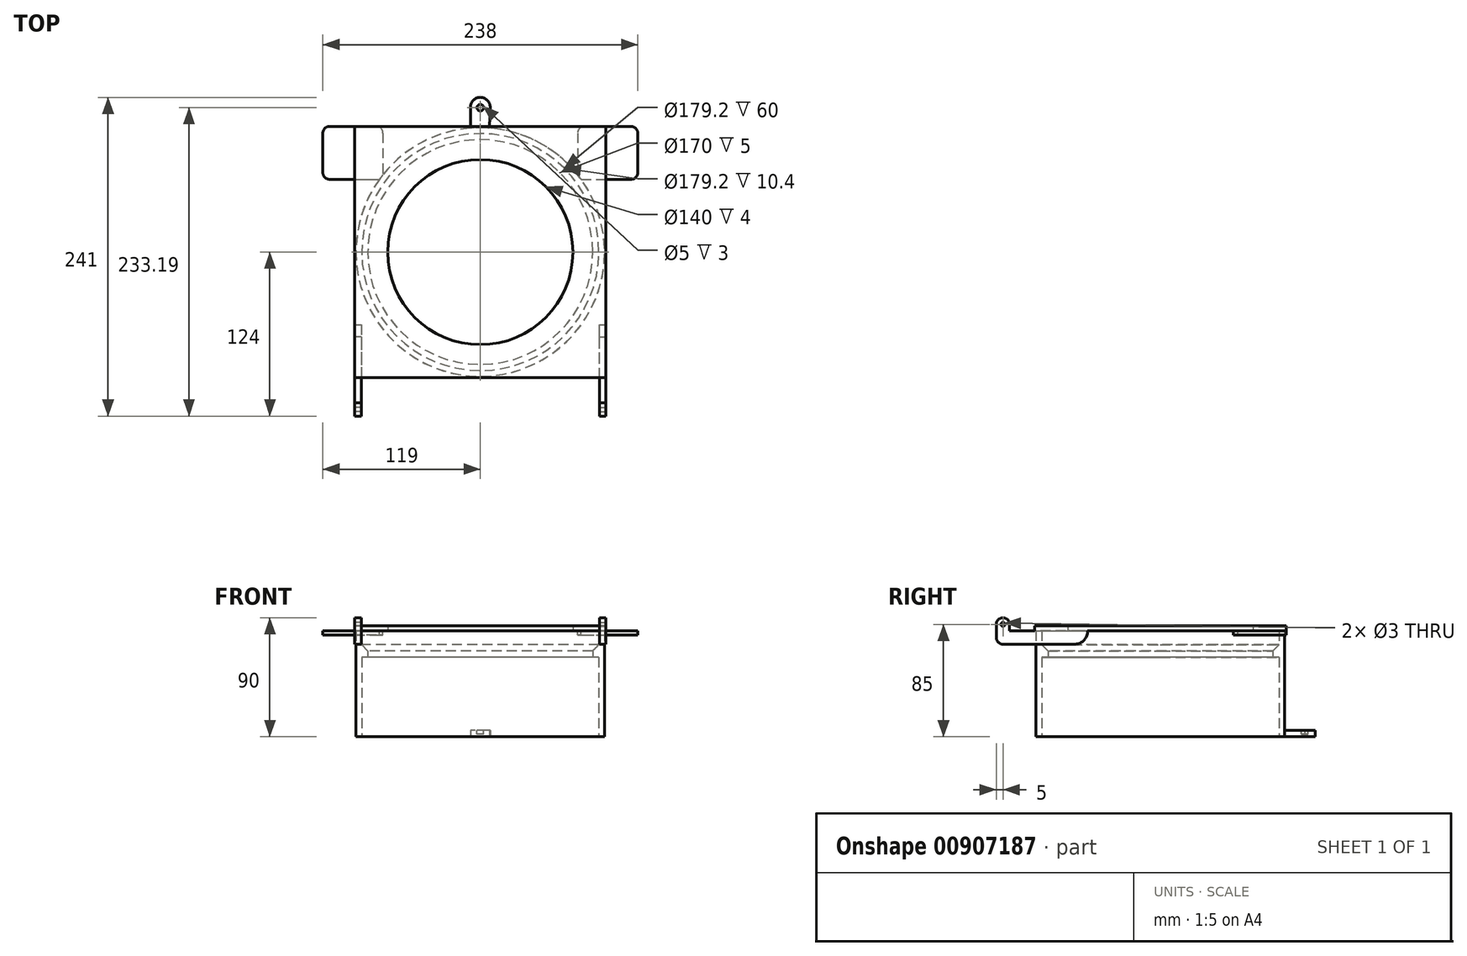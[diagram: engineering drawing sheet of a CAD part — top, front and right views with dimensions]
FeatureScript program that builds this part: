
annotation { "Feature Type Name" : "Feature", "Feature Type Description" : "" }
export const myFeature = defineFeature(function(context is Context, id is Id, definition is map)
    precondition{}
    {
        {
            var Q0;
            Q0=qCreatedBy(makeId("Top.planeOp"),FACE);
            var sketch = newSketch(context, id + "F0", { "sketchPlane" : qUnion([Q0])});
            skCircle(sketch, "E0", {"center": v(0, 0) * mm, "radius": 94 * mm});
            skCircle(sketch, "E1", {"center": v(0, 0) * mm, "radius": 89.6 * mm});
            skArc(sketch, "E2", {"start": v(7.5, 109.26) * mm, "mid": v(-0.04, 117) * mm, "end": v(-7.5, 109.19) * mm});
            skLineSegment(sketch, "E3", {"start": v(-7.5, 109.19) * mm, "end": v(-7.5, 93.7) * mm});
            skLineSegment(sketch, "E4", {"start": v(7.5, 109.26) * mm, "end": v(7, 93.74) * mm});
            skSolve(sketch);
        }
        {
            var Q0;
            Q0=makeQuery(id+"F0.imprint","IMPRINT",FACE,{"disambiguationData":[TD([[makeQuery(id+"F0.imprint","IMPRINT",EDGE,{"derivedFrom":sQuery(id+"F0.wireOp",EDGE,"E0")}),1.0]])]});
            extrude(context, id + "F1", {"entities" : qUnion([Q0]), "depth" : 60 * mm});
        }
        {
            var Q0;
            Q0=makeQuery(id+"F1.opExtrude","CAP_FACE",FACE,{"disambiguationData":[OSD([sQuery(id+"F0.wireOp",EDGE,"E0"),sQuery(id+"F0.wireOp",EDGE,"E1")])],"isStart":false});
            var sketch = newSketch(context, id + "F2", { "sketchPlane" : qUnion([Q0])});
            skCircle(sketch, "E5", {"center": v(0, 0) * mm, "radius": 94 * mm});
            skCircle(sketch, "E6", {"center": v(0, 0) * mm, "radius": 85 * mm});
            skSolve(sketch);
        }
        {
            var Q0;
            Q0=makeQuery(id+"F2.imprint","IMPRINT",FACE,{"disambiguationData":[TD([[makeQuery(id+"F2.imprint","IMPRINT",EDGE,{"derivedFrom":sQuery(id+"F2.wireOp",EDGE,"E6")}),-1.0]])]});
            var Q1;
            Q1=makeQuery(id+"F2.imprint","IMPRINT",FACE,{"disambiguationData":[TD([[makeQuery(id+"F2.imprint","IMPRINT",EDGE,{"derivedFrom":sQuery(id+"F2.wireOp",EDGE,"E5")}),1.0]])]});
            extrude(context, id + "F3", {"entities" : qUnion([Q0, Q1]), "operationType" : NewBodyOperationType.ADD, "depth" : 10 * mm});
        }
        {
            var Q0;
            Q0=makeQuery(id+"F3.opExtrude","CAP_FACE",FACE,{"disambiguationData":[OSD([sQuery(id+"F2.wireOp",EDGE,"E5"),sQuery(id+"F2.wireOp",EDGE,"E6")])],"isStart":false});
            var sketch = newSketch(context, id + "F4", { "sketchPlane" : qUnion([Q0])});
            skCircle(sketch, "E7", {"center": v(0, 0) * mm, "radius": 94 * mm});
            skCircle(sketch, "E8", {"center": v(0, 0) * mm, "radius": 89.6 * mm});
            skSolve(sketch);
        }
        {
            var Q0;
            Q0=makeQuery(id+"F4.imprint","IMPRINT",FACE,{"disambiguationData":[TD([[makeQuery(id+"F4.imprint","IMPRINT",EDGE,{"derivedFrom":sQuery(id+"F4.wireOp",EDGE,"E7")}),1.0]])]});
            extrude(context, id + "F5", {"entities" : qUnion([Q0]), "operationType" : NewBodyOperationType.ADD, "depth" : 10 * mm});
        }
        {
            var Q0;
            Q0=makeQuery(id+"F5.opExtrude","CAP_FACE",FACE,{"disambiguationData":[OSD([sQuery(id+"F4.wireOp",EDGE,"E7"),sQuery(id+"F4.wireOp",EDGE,"E8")])],"isStart":false});
            var sketch = newSketch(context, id + "F6", { "sketchPlane" : qUnion([Q0])});
            skLineSegment(sketch, "E9.bottom", {"start": v(95, -95) * mm, "end": v(-95, -95) * mm});
            skLineSegment(sketch, "E9.top", {"start": v(95, 95) * mm, "end": v(-95, 95) * mm});
            skLineSegment(sketch, "E9.left", {"start": v(95, -95) * mm, "end": v(95, 95) * mm});
            skLineSegment(sketch, "E9.right", {"start": v(-95, -95) * mm, "end": v(-95, 95) * mm});
            skPoint(sketch, "E9.middle", {"position": v(0, 0) * mm});
            skCircle(sketch, "E10", {"center": v(0, 0) * mm, "radius": 70 * mm});
            skSolve(sketch);
        }
        {
            var Q0;
            Q0=makeQuery(id+"F6.imprint","IMPRINT",FACE,{"disambiguationData":[TD([[makeQuery(id+"F6.imprint","IMPRINT",EDGE,{"derivedFrom":sQuery(id+"F6.wireOp",EDGE,"E9.bottom")}),-1.0]])]});
            var Q1;
            Q1=makeQuery(id+"F6.imprint","IMPRINT",FACE,{"disambiguationData":[TD([[makeQuery(id+"F6.imprint","IMPRINT",EDGE,{"derivedFrom":sQuery(id+"F6.wireOp",EDGE,"E10")}),-1.0]])]});
            var Q2;
            Q2=makeQuery(id+"F6.imprint","IMPRINT",FACE,{"disambiguationData":[TD([[makeQuery(id+"F6.imprint","IMPRINT",EDGE,{"derivedFrom":makeQuery(id+"F5.opExtrude","CAP_EDGE",EDGE,{"disambiguationData":[OSD([sQuery(id+"F4.wireOp",EDGE,"E7")])],"isStart":false})}),1.0]])]});
            extrude(context, id + "F7", {"entities" : qUnion([Q0, Q1, Q2]), "operationType" : NewBodyOperationType.ADD, "depth" : 4 * mm});
        }
        {
            var Q0;
            Q0=makeQuery(id+"F0.imprint","IMPRINT",FACE,{"disambiguationData":[TD([[makeQuery(id+"F0.imprint","IMPRINT",EDGE,{"derivedFrom":sQuery(id+"F0.wireOp",EDGE,"E2")}),1.0]])]});
            extrude(context, id + "F8", {"entities" : qUnion([Q0]), "operationType" : NewBodyOperationType.ADD, "depth" : 5 * mm});
        }
        {
            var Q0;
            Q0=makeQuery(id+"F8.opExtrude","CAP_FACE",FACE,{"disambiguationData":[OSD([sQuery(id+"F0.wireOp",EDGE,"E0"),sQuery(id+"F0.wireOp",EDGE,"E2"),sQuery(id+"F0.wireOp",EDGE,"E3"),sQuery(id+"F0.wireOp",EDGE,"E4")])],"isStart":false});
            var sketch = newSketch(context, id + "F9", { "sketchPlane" : qUnion([Q0])});
            skCircle(sketch, "E11", {"center": v(0, 109.19) * mm, "radius": 2.5 * mm});
            skSolve(sketch);
        }
        {
            var Q0;
            Q0=makeQuery(id+"F9.imprint","IMPRINT",FACE,{"disambiguationData":[TD([[makeQuery(id+"F9.imprint","IMPRINT",EDGE,{"derivedFrom":sQuery(id+"F9.wireOp",EDGE,"E11")}),1.0]])]});
            extrude(context, id + "F10", {"entities" : qUnion([Q0]), "operationType" : NewBodyOperationType.REMOVE, "oppositeDirection" : true, "depth" : 3 * mm});
        }
        {
            var Q0;
            Q0=makeQuery(id+"F3.opExtrude","CAP_EDGE",EDGE,{"disambiguationData":[OSD([sQuery(id+"F2.wireOp",EDGE,"E6")])],"isStart":false});
            chamfer(context, id + "F11", {"entities" : qUnion([Q0]), "width" : 5 * mm, "tangentPropagation" : true});
        }
        {
            var Q0;
            {var subQ0=sQuery(id+"F6.wireOp",EDGE,"E9.bottom");var subQ1=sQuery(id+"F6.wireOp",EDGE,"E9.top");var subQ2=sQuery(id+"F6.wireOp",EDGE,"E9.left");var subQ3=sQuery(id+"F6.wireOp",EDGE,"E9.right");Q0=makeQuery(id+"F7.boolean.opBoolean","SPLIT",FACE,{"disambiguationData":[TD([makeQuery(id+"F1.opExtrude","SWEPT_FACE",FACE,{"disambiguationData":[OSD([sQuery(id+"F0.wireOp",EDGE,"E0")])]})])],"derivedFrom":makeQuery(id+"F7.opExtrude","CAP_FACE",FACE,{"disambiguationData":[OSD([subQ0,subQ1,subQ2,subQ3,sQuery(id+"F6.wireOp",EDGE,"E10")])],"isStart":true})});}
            var sketch = newSketch(context, id + "F12", { "sketchPlane" : qUnion([Q0])});
            skLineSegment(sketch, "E12.bottom", {"start": v(95, -95) * mm, "end": v(114, -95) * mm});
            skLineSegment(sketch, "E12.top", {"start": v(95, -55) * mm, "end": v(114, -55) * mm});
            skLineSegment(sketch, "E12.right", {"start": v(119, -90) * mm, "end": v(119, -60) * mm});
            skPoint(sketch, "E13.visualSharp", {"position": v(119, -95) * mm});
            skArc(sketch, "E13.filletArc", {"start": v(114, -95) * mm, "mid": v(117.54, -93.54) * mm, "end": v(119, -90) * mm});
            skPoint(sketch, "E14.visualSharp", {"position": v(119, -55) * mm});
            skArc(sketch, "E14.filletArc", {"start": v(119, -60) * mm, "mid": v(117.54, -56.46) * mm, "end": v(114, -55) * mm});
            skLineSegment(sketch, "E15.bottom", {"start": v(95, -95) * mm, "end": v(78.59, -95) * mm});
            skLineSegment(sketch, "E15.top", {"start": v(95, -55) * mm, "end": v(73.59, -55) * mm});
            skLineSegment(sketch, "E15.right", {"start": v(73.59, -90) * mm, "end": v(73.59, -55) * mm});
            skPoint(sketch, "E16.visualSharp", {"position": v(73.59, -95) * mm});
            skArc(sketch, "E16.filletArc", {"start": v(73.59, -90) * mm, "mid": v(75.05, -93.54) * mm, "end": v(78.59, -95) * mm});
            skLineSegment(sketch, "E17.MirrorCS", {"start": v(-95, -95) * mm, "end": v(-114, -95) * mm});
            skLineSegment(sketch, "E18.MirrorCS", {"start": v(-95, -95) * mm, "end": v(-78.59, -95) * mm});
            skArc(sketch, "E19.MirrorCS", {"start": v(-73.59, -90) * mm, "mid": v(-75.05, -93.54) * mm, "end": v(-78.59, -95) * mm});
            skLineSegment(sketch, "E20.MirrorCS", {"start": v(-73.59, -90) * mm, "end": v(-73.59, -55) * mm});
            skLineSegment(sketch, "E21.MirrorCS", {"start": v(-95, -55) * mm, "end": v(-73.59, -55) * mm});
            skLineSegment(sketch, "E22.MirrorCS", {"start": v(-95, -55) * mm, "end": v(-114, -55) * mm});
            skArc(sketch, "E23.MirrorCS", {"start": v(-119, -60) * mm, "mid": v(-117.54, -56.46) * mm, "end": v(-114, -55) * mm});
            skLineSegment(sketch, "E24.MirrorCS", {"start": v(-119, -90) * mm, "end": v(-119, -60) * mm});
            skArc(sketch, "E25.MirrorCS", {"start": v(-114, -95) * mm, "mid": v(-117.54, -93.54) * mm, "end": v(-119, -90) * mm});
            skSolve(sketch);
        }
        {
            var Q0;
            {var subQ1=sQuery(id+"F12.wireOp",EDGE,"E12.bottom");Q0=makeQuery(id+"F12.imprint","IMPRINT",FACE,{"disambiguationData":[TD([[makeQuery(id+"F12.imprint","IMPRINT",EDGE,{"derivedFrom":subQ1}),1.0]])]});}
            var Q1;
            {var subQ8=sQuery(id+"F12.wireOp",EDGE,"E15.bottom");Q1=makeQuery(id+"F12.imprint","IMPRINT",FACE,{"disambiguationData":[TD([[makeQuery(id+"F12.imprint","IMPRINT",EDGE,{"derivedFrom":subQ8}),-1.0]])]});}
            var Q2;
            {var subQ8=sQuery(id+"F12.wireOp",EDGE,"E18.MirrorCS");Q2=makeQuery(id+"F12.imprint","IMPRINT",FACE,{"disambiguationData":[TD([[makeQuery(id+"F12.imprint","IMPRINT",EDGE,{"derivedFrom":subQ8}),-1.0]])]});}
            var Q3;
            {var subQ1=sQuery(id+"F12.wireOp",EDGE,"E17.MirrorCS");Q3=makeQuery(id+"F12.imprint","IMPRINT",FACE,{"disambiguationData":[TD([[makeQuery(id+"F12.imprint","IMPRINT",EDGE,{"derivedFrom":subQ1}),-1.0]])]});}
            extrude(context, id + "F13", {"entities" : qUnion([Q0, Q1, Q2, Q3]), "operationType" : NewBodyOperationType.ADD, "depth" : 3 * mm});
        }
        {
            var Q0;
            {var subQ0=sQuery(id+"F6.wireOp",EDGE,"E9.bottom");var subQ1=makeQuery(id+"F7.opExtrude","SWEPT_FACE",FACE,{"disambiguationData":[OSD([subQ0])]});var subQ9=makeQuery(id+"F1.opExtrude","SWEPT_FACE",FACE,{"disambiguationData":[OSD([sQuery(id+"F0.wireOp",EDGE,"E0")])]});var subQ10=sQuery(id+"F6.wireOp",EDGE,"E9.left");var subQ12=sQuery(id+"F6.wireOp",EDGE,"E9.right");var subQ14=sQuery(id+"F6.wireOp",EDGE,"E9.top");Q0=makeQuery(id+"F13.boolean.opBoolean","SPLIT",FACE,{"disambiguationData":[TD([subQ1])],"derivedFrom":makeQuery(id+"F7.boolean.opBoolean","SPLIT",FACE,{"disambiguationData":[TD([subQ9])],"derivedFrom":makeQuery(id+"F7.opExtrude","CAP_FACE",FACE,{"disambiguationData":[OSD([subQ0,subQ14,subQ10,subQ12,sQuery(id+"F6.wireOp",EDGE,"E10")])],"isStart":true})})});}
            var sketch = newSketch(context, id + "F14", { "sketchPlane" : qUnion([Q0])});
            skLineSegment(sketch, "E26.bottom", {"start": v(-95, 95) * mm, "end": v(-90, 95) * mm});
            skLineSegment(sketch, "E26.top", {"start": v(-95, 119) * mm, "end": v(-90, 119) * mm});
            skLineSegment(sketch, "E26.left", {"start": v(-95, 95) * mm, "end": v(-95, 119) * mm});
            skLineSegment(sketch, "E26.right", {"start": v(-90, 95) * mm, "end": v(-90, 119) * mm});
            skLineSegment(sketch, "E27.top", {"start": v(-95, 55) * mm, "end": v(-90, 55) * mm});
            skLineSegment(sketch, "E27.left", {"start": v(-95, 95) * mm, "end": v(-95, 55) * mm});
            skLineSegment(sketch, "E27.right", {"start": v(-90, 95) * mm, "end": v(-90, 55) * mm});
            skLineSegment(sketch, "E28.top", {"start": v(-95, 124) * mm, "end": v(-90, 124) * mm});
            skLineSegment(sketch, "E28.left", {"start": v(-95, 119) * mm, "end": v(-95, 124) * mm});
            skLineSegment(sketch, "E28.right", {"start": v(-90, 119) * mm, "end": v(-90, 124) * mm});
            skSolve(sketch);
        }
        {
            var Q0;
            Q0=qSketchRegion(id+"F14",true);
            extrude(context, id + "F15", {"entities" : qUnion([Q0]), "operationType" : NewBodyOperationType.ADD, "depth" : 10 * mm});
        }
        {
            var Q0;
            Q0=makeQuery(id+"F15.boolean.opBoolean","MERGE",FACE,{"derivedFrom":[makeQuery(id+"F7.opExtrude","SWEPT_FACE",FACE,{"disambiguationData":[OSD([sQuery(id+"F6.wireOp",EDGE,"E9.right")])]}),makeQuery(id+"F15.opExtrude","SWEPT_FACE",FACE,{"disambiguationData":[OSD([sQuery(id+"F14.wireOp",EDGE,"E26.left"),sQuery(id+"F14.wireOp",EDGE,"E27.left")])]})]});
            var sketch = newSketch(context, id + "F16", { "sketchPlane" : qUnion([Q0])});
            skArc(sketch, "E29", {"start": v(55, 80) * mm, "mid": v(58.27, 72.58) * mm, "end": v(65.95, 70) * mm});
            skSolve(sketch);
        }
        {
            var Q0;
            Q0=qSketchRegion(id+"F16",true);
            var Q1;
            {var subQ3=sQuery(id+"F6.wireOp",EDGE,"E9.right");var subQ5=sQuery(id+"F14.wireOp",EDGE,"E27.left");var subQ6=makeQuery(id+"F15.opExtrude","SWEPT_EDGE",EDGE,{"disambiguationData":[OSD([subQ3,sQuery(id+"F14.wireOp",EDGE,"E27.top"),subQ5])]});Q1=makeQuery(id+"F16.imprint","IMPRINT",FACE,{"disambiguationData":[TD([[makeQuery(id+"F16.imprint","IMPRINT",EDGE,{"derivedFrom":subQ6}),-1.0]])]});}
            extrude(context, id + "F17", {"entities" : qUnion([Q0, Q1]), "operationType" : NewBodyOperationType.REMOVE, "endBound" : BoundingType.UP_TO_NEXT, "oppositeDirection" : true, "depth" : 25 * mm});
        }
        {
            var Q0;
            Q0=makeQuery(id+"F15.opExtrude","CAP_EDGE",EDGE,{"disambiguationData":[OSD([sQuery(id+"F14.wireOp",EDGE,"E28.top")])],"isStart":false});
            fillet(context, id + "F18", {"entities" : qUnion([Q0]), "radius" : 5 * mm, "tangentPropagation" : true, "allowEdgeOverflow" : false});
        }
        {
            var Q0;
            Q0=makeQuery(id+"F15.boolean.opBoolean","MERGE",FACE,{"derivedFrom":[makeQuery(id+"F7.opExtrude","SWEPT_FACE",FACE,{"disambiguationData":[OSD([sQuery(id+"F6.wireOp",EDGE,"E9.right")])]}),makeQuery(id+"F15.opExtrude","SWEPT_FACE",FACE,{"disambiguationData":[OSD([sQuery(id+"F14.wireOp",EDGE,"E26.left"),sQuery(id+"F14.wireOp",EDGE,"E27.left"),sQuery(id+"F14.wireOp",EDGE,"E28.left")])]})]});
            var sketch = newSketch(context, id + "F19", { "sketchPlane" : qUnion([Q0])});
            skLineSegment(sketch, "E30.bottom", {"start": v(124, 80) * mm, "end": v(114, 80) * mm});
            skLineSegment(sketch, "E30.top", {"start": v(119, 90) * mm, "end": v(119, 90) * mm});
            skLineSegment(sketch, "E30.left", {"start": v(124, 80) * mm, "end": v(124, 85) * mm});
            skLineSegment(sketch, "E30.right", {"start": v(114, 80) * mm, "end": v(114, 85) * mm});
            skPoint(sketch, "E31.visualSharp", {"position": v(124, 90) * mm});
            skArc(sketch, "E31.filletArc", {"start": v(124, 85) * mm, "mid": v(122.54, 88.54) * mm, "end": v(119, 90) * mm});
            skPoint(sketch, "E32.visualSharp", {"position": v(114, 90) * mm});
            skArc(sketch, "E32.filletArc", {"start": v(119, 90) * mm, "mid": v(115.46, 88.54) * mm, "end": v(114, 85) * mm});
            skSolve(sketch);
        }
        {
            var Q0;
            Q0=makeQuery(id+"F19.imprint","IMPRINT",FACE,{"disambiguationData":[TD([[makeQuery(id+"F19.imprint","IMPRINT",EDGE,{"derivedFrom":sQuery(id+"F19.wireOp",EDGE,"E30.bottom")}),1.0]])]});
            extrude(context, id + "F20", {"entities" : qUnion([Q0]), "operationType" : NewBodyOperationType.ADD, "oppositeDirection" : true, "depth" : 5 * mm});
        }
        {
            var Q0;
            Q0=makeQuery(id+"F20.boolean.opBoolean","MERGE",FACE,{"derivedFrom":[makeQuery(id+"F15.boolean.opBoolean","MERGE",FACE,{"derivedFrom":[makeQuery(id+"F7.opExtrude","SWEPT_FACE",FACE,{"disambiguationData":[OSD([sQuery(id+"F6.wireOp",EDGE,"E9.right")])]}),makeQuery(id+"F15.opExtrude","SWEPT_FACE",FACE,{"disambiguationData":[OSD([sQuery(id+"F14.wireOp",EDGE,"E26.left"),sQuery(id+"F14.wireOp",EDGE,"E27.left"),sQuery(id+"F14.wireOp",EDGE,"E28.left")])]})]}),makeQuery(id+"F20.opExtrude","CAP_FACE",FACE,{"disambiguationData":[OSD([sQuery(id+"F19.wireOp",EDGE,"E30.bottom"),sQuery(id+"F19.wireOp",EDGE,"E30.left"),sQuery(id+"F19.wireOp",EDGE,"E30.right"),sQuery(id+"F19.wireOp",EDGE,"E31.filletArc"),sQuery(id+"F19.wireOp",EDGE,"E32.filletArc")])],"isStart":true})]});
            var sketch = newSketch(context, id + "F21", { "sketchPlane" : qUnion([Q0])});
            skCircle(sketch, "E33", {"center": v(119, 85) * mm, "radius": 1.5 * mm});
            skSolve(sketch);
        }
        {
            var Q0;
            Q0=makeQuery(id+"F21.imprint","IMPRINT",FACE,{"disambiguationData":[TD([[makeQuery(id+"F21.imprint","IMPRINT",EDGE,{"derivedFrom":sQuery(id+"F21.wireOp",EDGE,"E33")}),1.0]])]});
            extrude(context, id + "F22", {"entities" : qUnion([Q0]), "operationType" : NewBodyOperationType.REMOVE, "endBound" : BoundingType.UP_TO_NEXT, "oppositeDirection" : true, "depth" : 25 * mm});
        }
        {
            var Q0;
            Q0=makeQuery(id+"F7.opExtrude","SWEPT_FACE",FACE,{"disambiguationData":[OSD([sQuery(id+"F6.wireOp",EDGE,"E9.left")])]});
            var sketch = newSketch(context, id + "F23", { "sketchPlane" : qUnion([Q0])});
            skLineSegment(sketch, "E34.0.0", {"start": v(-124, 85) * mm, "end": v(-124, 75) * mm});
            skArc(sketch, "E34.0.1", {"start": v(-124, 75) * mm, "mid": v(-122.54, 71.46) * mm, "end": v(-119, 70) * mm});
            skLineSegment(sketch, "E34.0.2", {"start": v(-119, 70) * mm, "end": v(-64.13, 70) * mm});
            skArc(sketch, "E34.0.3", {"start": v(-64.13, 70) * mm, "mid": v(-57.63, 73.23) * mm, "end": v(-55, 80) * mm});
            skLineSegment(sketch, "E34.0.4", {"start": v(-55, 80) * mm, "end": v(-95, 80) * mm});
            skLineSegment(sketch, "E34.0.5", {"start": v(-95, 80) * mm, "end": v(-114, 80) * mm});
            skLineSegment(sketch, "E34.0.6", {"start": v(-114, 80) * mm, "end": v(-114, 85) * mm});
            skArc(sketch, "E34.0.7", {"start": v(-114, 85) * mm, "mid": v(-119, 90) * mm, "end": v(-124, 85) * mm});
            skCircle(sketch, "E35.0", {"center": v(-119, 85) * mm, "radius": 1.5 * mm});
            skSolve(sketch);
        }
        {
            var Q0;
            Q0=makeQuery(id+"F23.imprint","IMPRINT",FACE,{"disambiguationData":[TD([[makeQuery(id+"F23.imprint","IMPRINT",EDGE,{"derivedFrom":sQuery(id+"F23.wireOp",EDGE,"E34.0.0")}),1.0]])]});
            extrude(context, id + "F24", {"entities" : qUnion([Q0]), "operationType" : NewBodyOperationType.ADD, "oppositeDirection" : true, "depth" : 5 * mm});
        }
    });
